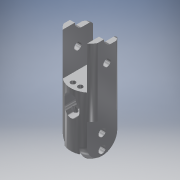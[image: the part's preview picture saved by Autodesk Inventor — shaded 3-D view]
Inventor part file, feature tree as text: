
AUTODESK INVENTOR PART (.ipt)
format: ipt  version: 2019 (Build 230136000, 136)  size: 211,968 bytes
history: imported  units: in
note: dims shown in document units (in); Inventor stores cm internally (conversion verified against a paired STEP export)
features: imported_body x1
ambient origin geometry x8: Origin, YZ Plane, XZ Plane, XY Plane, X Axis, Y Axis, Z Axis, Center Point
bodies: Solid1 (imported_parasolid)
feature tree (1):
  imported_body  NMx_Import_Brep_tag  [imported B-rep: ~7 faces, bbox_mm=[0.0, 2.7, 0.0]]
